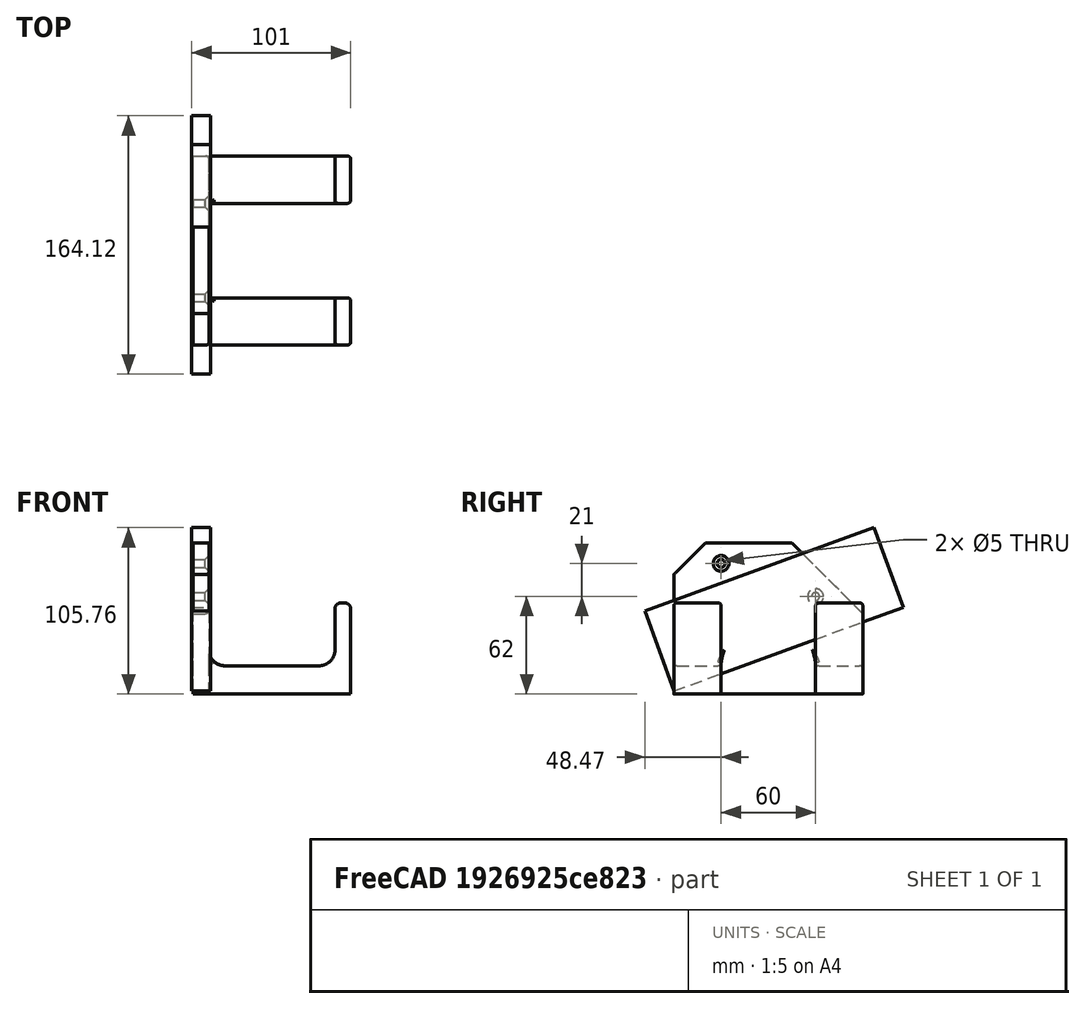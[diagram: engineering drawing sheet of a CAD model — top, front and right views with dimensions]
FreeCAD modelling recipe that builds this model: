
FCSTD DOCUMENT  (FreeCAD 0.18R16146 (Git))
Label: Angle Grinder Hook
License: All rights reserved
LicenseURL: http://en.wikipedia.org/wiki/All_rights_reserved
objects: Part::Box×6, Part::Fillet×5, Part::MultiFuse×3, Part::Chamfer×3, Part::Cylinder×2, Part::Cut×1
note: 20 computed .brp shape members not serialized (recipe doc carries the construction recipe); baked Part::Feature solids carry a one-line shape summary decoded from their .brp

FEATURE [Part::Box] Box002  label="Cube002"
  AttacherType = Attacher::AttachEngine3D
  Height = 40
  Length = 10
  Placement = pos=(70,0,10) rot=(0,0,1;0rad)
  Width = 30
FEATURE [Part::Box] Box001  label="Cube001"
  AttacherType = Attacher::AttachEngine3D
  Height = 96
  Length = 10
  Placement = pos=(-20,0,-8) rot=(1,0,0;0rad)
  Width = 120
FEATURE [Part::Box] Box003  label="Cube003"
  AttacherType = Attacher::AttachEngine3D
  Height = 18
  Length = 90
  Placement = pos=(-10,0,-8) rot=(0,0,1;0rad)
  Width = 30
FEATURE [Part::Box] Box004  label="Cube004"
  AttacherType = Attacher::AttachEngine3D
  Height = 40
  Length = 10
  Placement = pos=(70,90,10) rot=(0,0,1;0rad)
  Width = 30
FEATURE [Part::Box] Box005  label="Cube005"
  AttacherType = Attacher::AttachEngine3D
  Height = 18
  Length = 90
  Placement = pos=(-10,90,-8) rot=(0,0,1;0rad)
  Width = 30
FEATURE [Part::MultiFuse] Fusion
  Shapes = -> [Box002,Box004,Box003,Box005]
FEATURE [Part::Box] Box  label="Cube"
  AttacherType = Attacher::AttachEngine3D
  Height = 54
  Length = 12
  Placement = pos=(-21,0,-6) rot=(1,0,0;0.349066rad)
  Width = 155
FEATURE [Part::Cylinder] Cylinder
  Angle = 360
  AttacherType = Attacher::AttachEngine3D
  Height = 20
  Placement = pos=(-24,30,87) rot=(0,1,0;1.5708rad)
  Radius = 2.5
FEATURE [Part::Cylinder] Cylinder001
  Angle = 360
  AttacherType = Attacher::AttachEngine3D
  Height = 20
  Placement = pos=(-24,90,66) rot=(0,1,0;1.5708rad)
  Radius = 2.5
FEATURE [Part::MultiFuse] Fusion001
  Shapes = -> [Fusion,Box001]
FEATURE [Part::MultiFuse] Fusion002
  Placement = pos=(0,0,-12) rot=(0,0,1;0rad)
  Shapes = -> [Cylinder,Cylinder001]
FEATURE [Part::Cut] Cut
  Base = -> Fusion001
  Tool = -> Fusion002
FEATURE [Part::Chamfer] Chamfer
  Base = -> Cut
  Edges = 2 edges r=2.5: [Edge19,Edge21]
FEATURE [Part::Fillet] Fillet
  Base = -> Chamfer
  Edges = 2 edges r=10: [Edge31,Edge37]
FEATURE [Part::Fillet] Fillet001
  Base = -> Fillet
  Edges = 2 edges r=10: [Edge3,Edge18]
FEATURE [Part::Chamfer] Chamfer001
  Base = -> Fillet001
  Edges = 1 edges r=45: [Edge47]
FEATURE [Part::Chamfer] Chamfer002
  Base = -> Chamfer001
  Edges = 1 edges r=20: [Edge16]
FEATURE [Part::Fillet] Fillet002
  Base = -> Chamfer002
  Edges = 4 edges r=4: [Edge91,Edge92,Edge93,Edge94]
FEATURE [Part::Fillet] Fillet003
  Base = -> Fillet002
  Edges = 2 edges r=2: [Edge21,Edge41]
FEATURE [Part::Fillet] Fillet004
  Base = -> Fillet003
  Edges = 4 edges r=2: [Edge3,Edge17,Edge92,Edge96]
